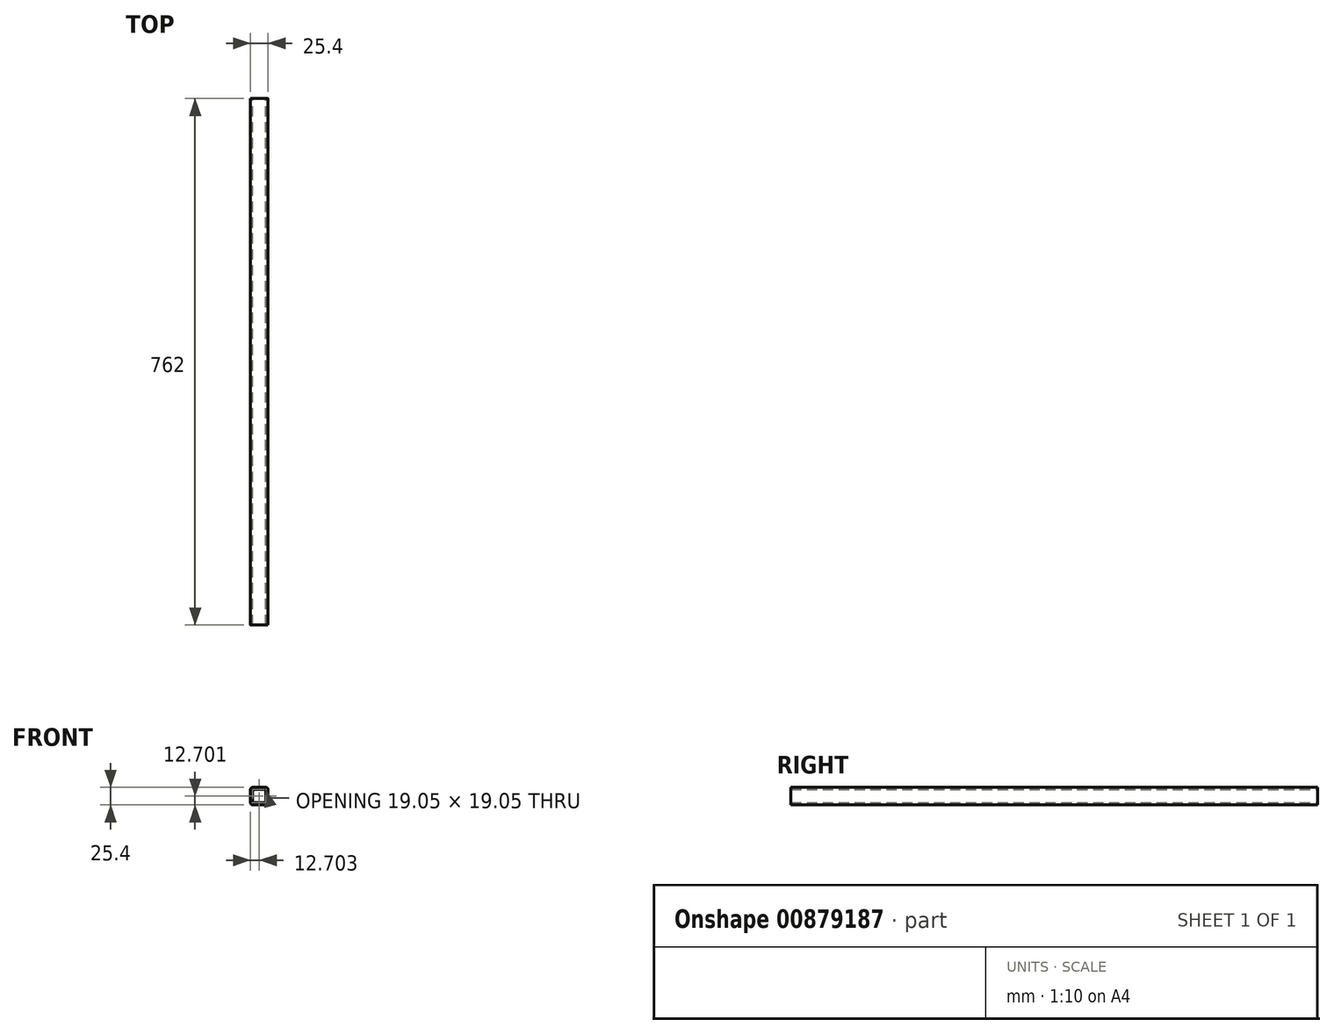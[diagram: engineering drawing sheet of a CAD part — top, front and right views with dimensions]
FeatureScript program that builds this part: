
annotation { "Feature Type Name" : "Feature", "Feature Type Description" : "" }
export const myFeature = defineFeature(function(context is Context, id is Id, definition is map)
    precondition{}
    {
        {
            var Q0;
            Q0=qCreatedBy(makeId("Front.planeOp"),FACE);
            var sketch = newSketch(context, id + "F0", { "sketchPlane" : qUnion([Q0])});
            skLineSegment(sketch, "E0.bottom", {"start": v(9.92, -12.2) * mm, "end": v(-9.13, -12.2) * mm});
            skLineSegment(sketch, "E0.top", {"start": v(9.92, 13.2) * mm, "end": v(-9.13, 13.2) * mm});
            skLineSegment(sketch, "E0.left", {"start": v(13.1, -9.03) * mm, "end": v(13.1, 10.02) * mm});
            skLineSegment(sketch, "E0.right", {"start": v(-12.3, -9.03) * mm, "end": v(-12.3, 10.02) * mm});
            skLineSegment(sketch, "E1.bottom", {"start": v(6.74, -9.03) * mm, "end": v(-5.96, -9.03) * mm});
            skLineSegment(sketch, "E1.top", {"start": v(6.74, 10.02) * mm, "end": v(-5.96, 10.02) * mm});
            skLineSegment(sketch, "E1.left", {"start": v(9.92, -5.86) * mm, "end": v(9.92, 6.84) * mm});
            skLineSegment(sketch, "E1.right", {"start": v(-9.13, -5.86) * mm, "end": v(-9.13, 6.84) * mm});
            skPoint(sketch, "E2.visualSharp", {"position": v(9.92, 10.02) * mm});
            skArc(sketch, "E2.filletArc", {"start": v(9.92, 6.84) * mm, "mid": v(8.99, 9.09) * mm, "end": v(6.74, 10.02) * mm});
            skPoint(sketch, "E3.visualSharp", {"position": v(-9.13, 10.02) * mm});
            skArc(sketch, "E3.filletArc", {"start": v(-5.96, 10.02) * mm, "mid": v(-8.2, 9.09) * mm, "end": v(-9.13, 6.84) * mm});
            skPoint(sketch, "E4.visualSharp", {"position": v(-9.13, -9.03) * mm});
            skArc(sketch, "E4.filletArc", {"start": v(-9.13, -5.86) * mm, "mid": v(-8.2, -8.1) * mm, "end": v(-5.96, -9.03) * mm});
            skPoint(sketch, "E5.visualSharp", {"position": v(9.92, -9.03) * mm});
            skArc(sketch, "E5.filletArc", {"start": v(6.74, -9.03) * mm, "mid": v(8.99, -8.1) * mm, "end": v(9.92, -5.86) * mm});
            skPoint(sketch, "E6.visualSharp", {"position": v(13.1, 13.2) * mm});
            skArc(sketch, "E6.filletArc", {"start": v(13.1, 10.02) * mm, "mid": v(12.16, 12.26) * mm, "end": v(9.92, 13.2) * mm});
            skPoint(sketch, "E7.visualSharp", {"position": v(-12.3, 13.2) * mm});
            skArc(sketch, "E7.filletArc", {"start": v(-9.13, 13.2) * mm, "mid": v(-11.38, 12.26) * mm, "end": v(-12.3, 10.02) * mm});
            skPoint(sketch, "E8.visualSharp", {"position": v(-12.3, -12.2) * mm});
            skArc(sketch, "E8.filletArc", {"start": v(-12.3, -9.03) * mm, "mid": v(-11.38, -11.28) * mm, "end": v(-9.13, -12.2) * mm});
            skPoint(sketch, "E9.visualSharp", {"position": v(13.1, -12.2) * mm});
            skArc(sketch, "E9.filletArc", {"start": v(9.92, -12.2) * mm, "mid": v(12.16, -11.28) * mm, "end": v(13.1, -9.03) * mm});
            skSolve(sketch);
        }
        {
            var Q0;
            Q0=qSketchRegion(id+"F0",true);
            extrude(context, id + "F1", {"entities" : qUnion([Q0]), "depth" : 762 * mm, "offsetDistance" : 25.4 * mm});
        }
    });
